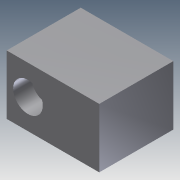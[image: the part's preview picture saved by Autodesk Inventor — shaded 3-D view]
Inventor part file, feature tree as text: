
AUTODESK INVENTOR PART (.ipt)
format: ipt  version: 2011 (Build 150239000, 239)  size: 81,408 bytes
history: native  units: in
note: dims shown in document units (in); Inventor stores cm internally (conversion verified against a paired STEP export)
features: extrude x2, sketch x2
ambient origin geometry x8: Origin, YZ Plane, XZ Plane, XY Plane, X Axis, Y Axis, Z Axis, Center Point
bodies: Solid1 (feature_tree)
feature tree (4):
  extrude  "Extrusion1"  Depth=1.2598in
  extrude  "Extrusion2"  Depth=0.4528in
  sketch  "Sketch1"  dims[d0=1.9685in d1=1.2598in]
  sketch  "Sketch2"  dims[d2=1.5748in d3=0.0in d4=0.4528in d5=0.6299in d6=0.3937in d7=0.0in]
